# Revit family: PRD_FrankeWS_ShwrThrmsttcVlvs_F3SSelf-closingStraight-wayValve_F3SV2009
name_source: partatom
category: Plumbing Fixtures
revit_build: Autodesk Revit 2018 (Build: 20190510_1515(x64)
units: mm (PartAtom-declared; Revit-internal decimal feet)

## family parameters
Cut with Voids When Loaded = Yes
Host = Face
OmniClass Number = 23.45.05.14.99
OmniClass Title = Other Sanitary Washing Plumbing Fixtures
Part Type = Normal
Room Calculation Point = No
Round Connector Dimension = Use Diameter
Shared = No

## types (1)
- F3SV2009
    AdditionalConnections = No
    AdjustableFlowTime = Yes
    AssetType = Fixed
    BIMObjectName = PRD_AR_ShowerThermostaticValves_F3SSelf-closingStraight-wayValve_F3SV2009
    CalculationFlowRateColdWater = 0.30 liter per second
    Category = Pr_40_20_87_80, Shower thermostatic valves
    Circulation = No
    CloseOffRating = 0.0 Pa
    Color = Chrome
    ConnectionWithPayWaterDispenser = Not possible
    Default Elevation = 850 mm  [stored 2.78871 ft]
    Description = F3S Self-closing straight-way valve DN 20 for in-wall mounting, for shower facilities. Self-closing functional part, hydraulically controlled, piston-free design, automatic closing, adjustable flow duration. For connection to pre-mixed hot water or cold water. Housing including replaceable valve seat, with interior thread G 3/4, visible parts made of high-polished chrome-plated brass. With rosette, depth adjustability 15 mm.
    DiameterNominal = 20.000 mm
    DurationUnit = year
    Features = For connection to pre-mixed hot water or cold water. Visible parts made of high-polished chrome-plated brass.
    Finish = Polished chrome
    FlowCoefficient = 0
    FlowColdWater = 0.3 L/s
    FlowRateMaximum = 1.25 L/s at 3 bar
    FunctionalPrinciple = Hydraulic self-closing
    GrossWeight = 0.65 kg
    HygieneFlushing = No
    IfcExportAs = IfcValveType
    IfcExportType = USERDEFINED
    InletSize = G3-4
    Manufacturer = KWC Group AG
    ManufacturerName = KWC Group AG
    ManufacturerURL = www.kwc.com
    Material = Brass
    MaximumFlowTime = 30.00 seconds
    MinimumFlowPressure = 1.00 bar
    MinimumFlowTime = 5.00 seconds
    Model = F3SV2009
    ModelNumber = 2030053188
    ModelReference = F3SV2009
    NBSDescription = Shower mixers
    NBSReference = 45-35-70/335
    Name = F3S self-closing straight-way valve F3SV2009
    NetWeight = 0.60 kg
    NominalDepth = 0 mm  [stored 0 ft]
    NominalHeight = 80 mm  [stored 0.262467 ft]
    NominalWidth = 80 mm  [stored 0.262467 ft]
    PositionOfWaterConnection = From bottom
    ProductCode = 210.0630.554
    ProductInformation = https://pim.kwc.com
    ProtectiveShutdown = No
    ShowerPipeDraining = No
    SoundInsulation = No
    Status = New
    TailorMade = No
    TapMaterial = PRD_AR_ChromatedBrass_HighPolished
    TestPressure = 0.0 Pa
    ThermalDisinfection = No
    TypeOfMixing = No mixing
    TypeOfMounting = In-wall installation without box
    TypeOfOperation = Manual operation
    TypeOfShower = In-wall fitting
    URL = www.kwc.com
    Uniclass2015Code = Pr_40_20_87_80
    Uniclass2015Title = Shower thermostatic valves
    Uniclass2015Version = Products v1.17
    ValveMechanism = OTHER
    ValveOperation = HYDRAULIC
    ValvePattern = STRAIGHT_2_PORT
    Version = 1
    WarrantyDurationUnit = year
    WorkingPressure = 0.0 Pa

note: [stored X ft] marks values corroborated as IEEE doubles in the binary element streams (Revit-internal decimal feet)

## geometry (parser evidence)
native form markers: Sweep x3
no freeform markers — native parametric forms only
